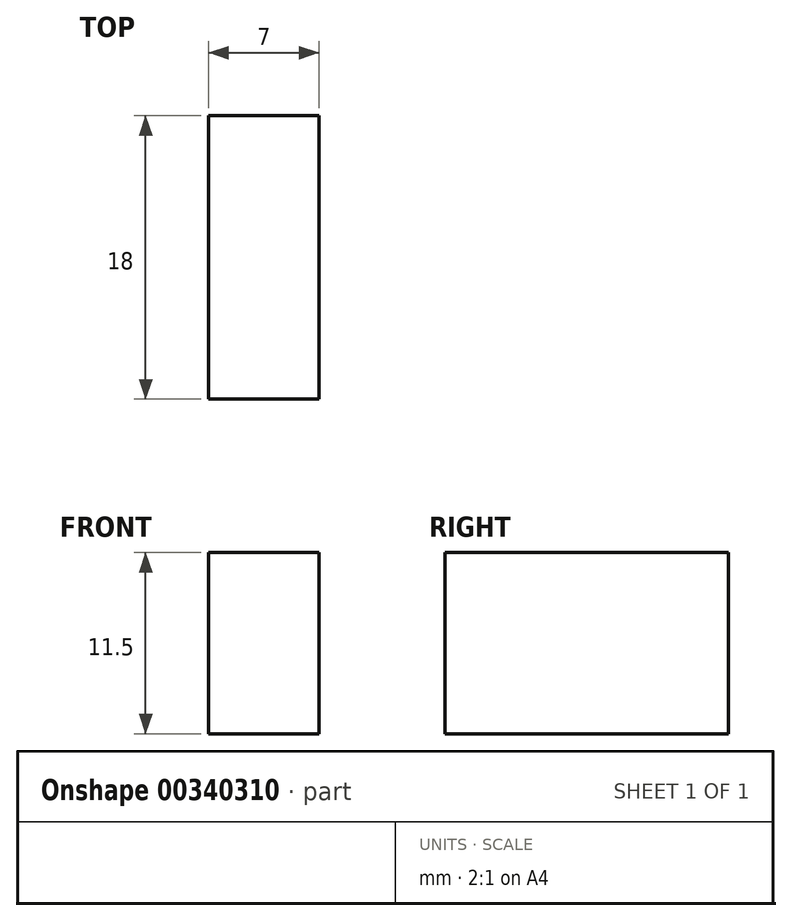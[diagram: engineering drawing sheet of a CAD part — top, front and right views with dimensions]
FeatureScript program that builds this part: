
annotation { "Feature Type Name" : "Feature", "Feature Type Description" : "" }
export const myFeature = defineFeature(function(context is Context, id is Id, definition is map)
    precondition{}
    {
        {
            var Q0;
            Q0=qCreatedBy(makeId("Front.planeOp"),FACE);
            var sketch = newSketch(context, id + "F0", { "sketchPlane" : qUnion([Q0])});
            skLineSegment(sketch, "E0.bottom", {"start": v(3.5, 5.75) * mm, "end": v(-3.5, 5.75) * mm});
            skLineSegment(sketch, "E0.top", {"start": v(3.5, -5.75) * mm, "end": v(-3.5, -5.75) * mm});
            skLineSegment(sketch, "E0.left", {"start": v(3.5, 5.75) * mm, "end": v(3.5, -5.75) * mm});
            skLineSegment(sketch, "E0.right", {"start": v(-3.5, 5.75) * mm, "end": v(-3.5, -5.75) * mm});
            skPoint(sketch, "E0.middle", {"position": v(0, 0) * mm});
            skSolve(sketch);
        }
        {
            var Q0;
            Q0 = qSketchRegion(id + "F0", true);
            extrude(context, id + "F1", {"entities" : qUnion([Q0]), "depth" : 18 * mm});
        }
    });
